# Revit family: WAGNER_Устройство_сбора_конденсата
name_source: partatom
category: Арматура трубопроводов
revit_build: Autodesk Revit 2017 (Build: 20190508_0315(x64)
units: mm (PartAtom-declared; Revit-internal decimal feet)

## family parameters
Всегда вертикально = Да
Заголовок OmniClass = Water Heated and Cooled Terminal Heating and Cooling Units
На основе рабочей плоскости = Нет
Номер OmniClass = 23.75.70.17
Общий = Да
При загрузке вырезать с полостями = Нет
Размер круглого соединителя = Использовать диаметр
Тип детали = Нормальный

## types (1)
- Typ KA-1
    ADSK_URL документации изделия = https://ru.wagnergroup.com
    ADSK_URL страницы изделия = https://ru.wagnergroup.com
    ADSK_Версия Revit = Revit 2017
    ADSK_Версия семейства = Версия 1
    ADSK_Дата изменения = 18.07.20
    ADSK_Единица измерения = шт.
    ADSK_Завод-изготовитель = WAGNER
    ADSK_Код изделия = -
    ADSK_Марка = Typ KA-1
    ADSK_Материал = WAGNER_Устройство_сбора_конденсата
    ADSK_Наименование = Устройство сбора конденсата
    ADSK_Наименование краткое = Устройство сбора конденсата
    ADSK_Размер_Высота = 50 мм
    ADSK_Размер_Длина = 660 мм
    ADSK_Размер_Ширина = 50 мм
    COBie Category = Moisture Instruments
    Masterformat Code = 23 09 23.19
    Masterformat Title = Moisture Instruments
    OmniClass Code = 23.75.70.17
    OmniClass Title = Water Heated and Cooled Terminal Heating and Coolinh Units
    UNSPSC Code = 41110000
    UNSPSC Title = Measuring and observing and testing instruments
    URL = www.wagner-russia.com
    Uniclass Code = Ss_55_40
    Uniclass Title = Steam distribution and supply systems
    WAGNER_Variation = 1
    WAGNER_Артикул = AD-10-0647
    WAGNER_Название = Устройство сбора конденсата
    WAGNER_Тип = Typ KA-1
    bimon.ru = bimon.ru
    Изготовитель = WAGNER
    Описание = Устройство сбора конденсата
